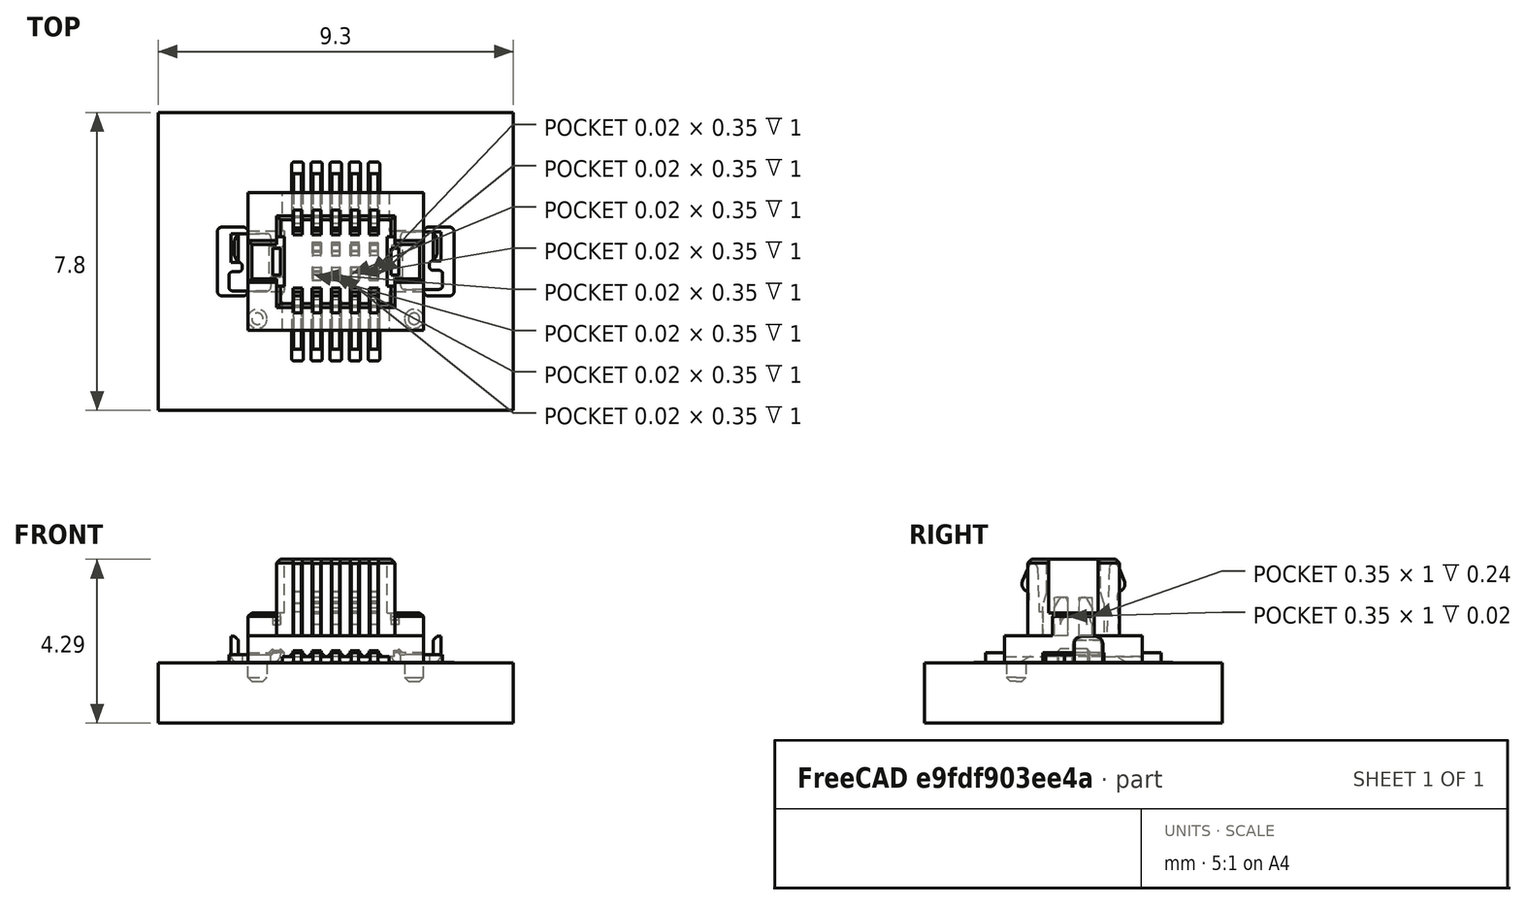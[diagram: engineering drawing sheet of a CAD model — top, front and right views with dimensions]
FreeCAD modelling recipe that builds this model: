
FCSTD DOCUMENT  (FreeCAD 1.0R39285 (Git))
Label: 10132798-012100LF
License: All rights reserved
LicenseURL: https://en.wikipedia.org/wiki/All_rights_reserved
objects: Part::Feature×6, Sketcher::SketchObject×3, App::DocumentObjectGroup×1
note: 12 computed .brp shape members not serialized (recipe doc carries the construction recipe); baked Part::Feature solids carry a one-line shape summary decoded from their .brp

FEATURE [Part::Feature] Shape001  label="topPads"
  Placement = pos=(0,0,-0.01) rot=(0,0,1;0rad)
  shape: bbox 6.2 x 5.2 x 0.01 mm, 120 faces, 12 solids (baked)
FEATURE [Part::Feature] Shape  label="F.SilkS_outline_"
  Placement = pos=(0,0,0.01) rot=(0,0,1;0rad)
  shape: bbox 4.7 x 0.4 x 2e-07 mm, 0 faces, 0 solids (baked)
FEATURE [Sketcher::SketchObject] _F_SilkS__sketch  label="F.SilkS_"
  ArcFitTolerance = 1e-06
  FullyConstrained = false
  MakeInternals = false
  Placement = pos=(0,0,0.01) rot=(0,0,1;0rad)
  sketch-geometry (4):
    g0: LineSegment StartX=-2.3 StartY=1.8 StartZ=0 EndX=-2 EndY=1.8 EndZ=0
    g1: LineSegment StartX=-2.3 StartY=1.5 StartZ=0 EndX=-2.3 EndY=1.8 EndZ=0
    g2: LineSegment StartX=2.3 StartY=1.8 StartZ=0 EndX=2 EndY=1.8 EndZ=0
    g3: LineSegment StartX=2.3 StartY=1.8 StartZ=0 EndX=2.3 EndY=1.5 EndZ=0
FEATURE [Part::Feature] Shape002  label="F.Fab_outline_"
  Placement = pos=(0,0,0.01) rot=(0,0,1;0rad)
  shape: bbox 4.65 x 3.65 x 2e-07 mm, 0 faces, 0 solids (baked)
FEATURE [Sketcher::SketchObject] _F_Fab__sketch  label="F.Fab_"
  ArcFitTolerance = 1e-06
  FullyConstrained = false
  MakeInternals = false
  Placement = pos=(0,0,0.01) rot=(0,0,1;0rad)
  sketch-geometry (4):
    g0: LineSegment StartX=-2.3 StartY=1.8 StartZ=0 EndX=-2.3 EndY=-1.8 EndZ=0
    g1: LineSegment StartX=-2.3 StartY=-1.8 StartZ=0 EndX=2.3 EndY=-1.8 EndZ=0
    g2: LineSegment StartX=2.3 StartY=-1.8 StartZ=0 EndX=2.3 EndY=1.8 EndZ=0
    g3: LineSegment StartX=2.3 StartY=1.8 StartZ=0 EndX=-2.3 EndY=1.8 EndZ=0
  constraints (4):
    c: Coincident(g0,g1)
    c: Coincident(g1,g2)
    c: Coincident(g2,g3)
    c: Coincident(g3,g0)
FEATURE [Part::Feature] Shape003  label="Edge.Cuts_outline_"
  Placement = pos=(0,0,0.01) rot=(0,0,1;0rad)
  shape: bbox 4.85 x 0.75 x 2e-07 mm, 0 faces, 0 solids (baked)
FEATURE [Sketcher::SketchObject] _Edge_Cuts__sketch  label="Edge.Cuts_"
  ArcFitTolerance = 1e-06
  FullyConstrained = false
  MakeInternals = false
  Placement = pos=(0,0,0.01) rot=(0,0,1;0rad)
  sketch-geometry (2):
    g0: Circle CenterX=-2.05 CenterY=-1.5 CenterZ=0 NormalX=0 NormalY=0 NormalZ=1 AngleXU=0 Radius=0.35
    g1: Circle CenterX=2.05 CenterY=-1.5 CenterZ=0 NormalX=0 NormalY=0 NormalZ=1 AngleXU=0 Radius=0.35
FEATURE [Part::Feature] PCB
  shape: bbox 9.3 x 7.8 x 1.58 mm, 6 faces (baked)
FEATURE [App::DocumentObjectGroup] Group  label="10132798-012100LF-fp"
  Group = -> [Shape001,_F_SilkS__sketch,Shape,_F_Fab__sketch,Shape002,_Edge_Cuts__sketch,Shape003,PCB]
FEATURE [Part::Feature] Shape127  label="10132798-012100LF_ASM"
  shape: bbox 5.6 x 4.6 x 3.2 mm, 566 faces (baked)
